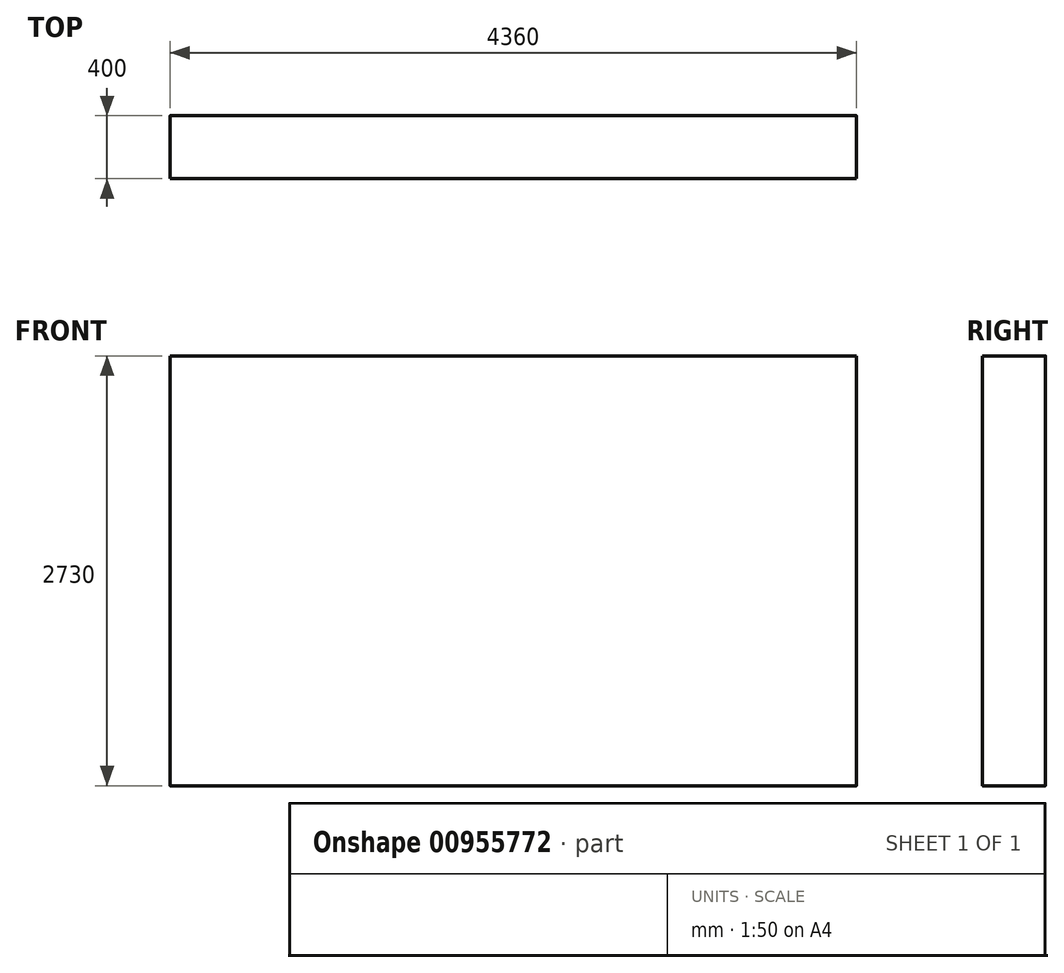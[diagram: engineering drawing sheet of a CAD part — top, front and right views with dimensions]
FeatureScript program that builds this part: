
annotation { "Feature Type Name" : "Feature", "Feature Type Description" : "" }
export const myFeature = defineFeature(function(context is Context, id is Id, definition is map)
    precondition{}
    {
        {
            var Q0;
            Q0=qCreatedBy(makeId("Front.planeOp"),FACE);
            var sketch = newSketch(context, id + "F0", { "sketchPlane" : qUnion([Q0])});
            skLineSegment(sketch, "E0.bottom", {"start": v(-293.72, 2730) * mm, "end": v(4066.28, 2730) * mm});
            skLineSegment(sketch, "E0.top", {"start": v(-293.72, 0) * mm, "end": v(4066.28, 0) * mm});
            skLineSegment(sketch, "E0.left", {"start": v(-293.72, 2730) * mm, "end": v(-293.72, 0) * mm});
            skLineSegment(sketch, "E0.right", {"start": v(4066.28, 2730) * mm, "end": v(4066.28, 0) * mm});
            skSolve(sketch);
        }
        {
            var Q0;
            Q0 = qSketchRegion(id + "F0", true);
            extrude(context, id + "F1", {"entities" : qUnion([Q0]), "depth" : 400 * mm, "offsetDistance" : 25.4 * mm});
        }
        {
            var Q0;
            Q0=makeQuery(id+"F1.opExtrude","CAP_EDGE",EDGE,{"disambiguationData":[OSD([sQuery(id+"F0.wireOp",EDGE,"E0.top")])],"isStart":false});
            fillet(context, id + "F2", {"entities" : qUnion([Q0]), "radius" : ((0.5 * sqrt(2)) / 2) * mm, "tangentPropagation" : true, "allowEdgeOverflow" : false});
        }
        {
            var Q0;
            Q0=makeQuery(id+"F1.opExtrude","CAP_EDGE",EDGE,{"disambiguationData":[OSD([sQuery(id+"F0.wireOp",EDGE,"E0.top")])],"isStart":true});
            fillet(context, id + "F3", {"entities" : qUnion([Q0]), "radius" : ((0.5 * sqrt(2)) / 2) * mm, "tangentPropagation" : true, "allowEdgeOverflow" : false});
        }
        {
            var Q0;
            Q0=makeQuery(id+"F1.opExtrude","CAP_EDGE",EDGE,{"disambiguationData":[OSD([sQuery(id+"F0.wireOp",EDGE,"E0.bottom")])],"isStart":true});
            fillet(context, id + "F4", {"entities" : qUnion([Q0]), "radius" : ((.5 * sqrt(2)) / 2) * mm, "tangentPropagation" : true, "allowEdgeOverflow" : false});
        }
    });
